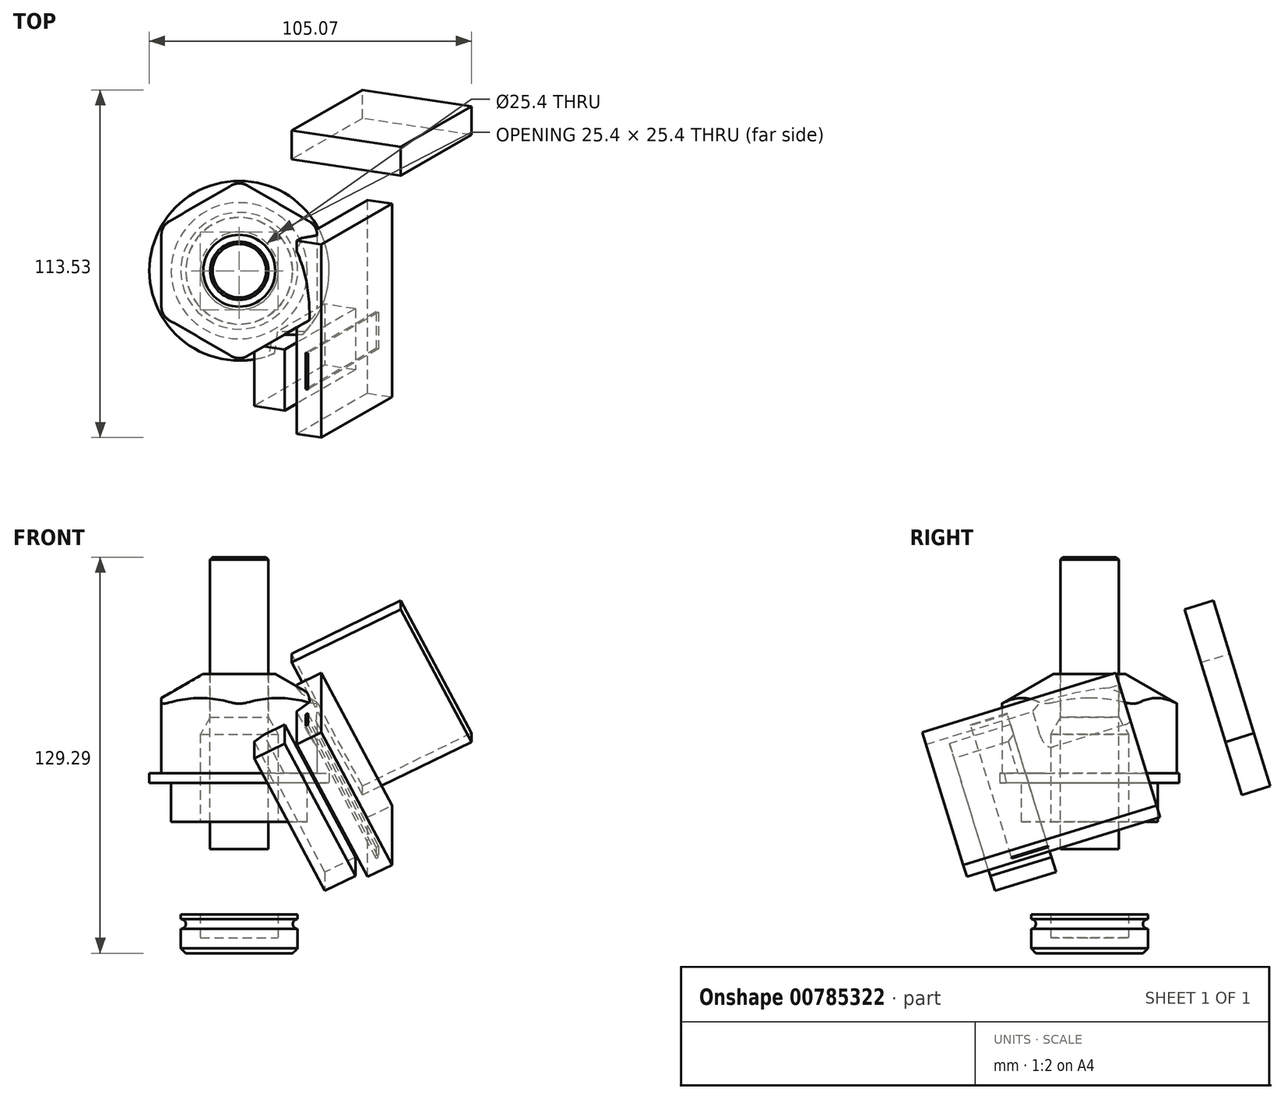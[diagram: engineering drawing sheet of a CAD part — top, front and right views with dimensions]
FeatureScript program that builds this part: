
annotation { "Feature Type Name" : "Feature", "Feature Type Description" : "" }
export const myFeature = defineFeature(function(context is Context, id is Id, definition is map)
    precondition{}
    {
        {
            var Q0;
            Q0=qCreatedBy(makeId("Top.planeOp"),FACE);
            var sketch = newSketch(context, id + "F0", { "sketchPlane" : qUnion([Q0])});
            skCircle(sketch, "E0", {"center": v(0, 0) * mm, "radius": 29.33 * mm});
            skLineSegment(sketch, "E1", {"start": v(0, 29.33) * mm, "end": v(0, -29.33) * mm, "construction": true});
            skLineSegment(sketch, "E2", {"start": v(-25.4, 14.66) * mm, "end": v(25.4, -14.66) * mm, "construction": true});
            skLineSegment(sketch, "E3", {"start": v(-25.4, -14.66) * mm, "end": v(25.4, 14.66) * mm, "construction": true});
            skLineSegment(sketch, "E4", {"start": v(-25.4, 14.66) * mm, "end": v(0, 29.33) * mm});
            skLineSegment(sketch, "E5", {"start": v(0, 29.33) * mm, "end": v(25.4, 14.66) * mm});
            skLineSegment(sketch, "E6", {"start": v(25.4, 14.66) * mm, "end": v(25.4, -14.66) * mm});
            skLineSegment(sketch, "E7", {"start": v(25.4, -14.66) * mm, "end": v(0, -29.33) * mm});
            skLineSegment(sketch, "E8", {"start": v(0, -29.33) * mm, "end": v(-25.4, -14.66) * mm});
            skLineSegment(sketch, "E9", {"start": v(-25.4, -14.66) * mm, "end": v(-25.4, 14.66) * mm});
            skCircle(sketch, "E10", {"center": v(0, 0) * mm, "radius": 7.94 * mm});
            skSolve(sketch);
        }
        {
            var Q0;
            Q0=makeQuery(id+"F0.imprint","IMPRINT",FACE,{"disambiguationData":[TD([[makeQuery(id+"F0.imprint","IMPRINT",EDGE,{"derivedFrom":sQuery(id+"F0.wireOp",EDGE,"E10")}),1.0]])]});
            var Q1;
            Q1=makeQuery(id+"F0.imprint","IMPRINT",FACE,{"disambiguationData":[TD([[makeQuery(id+"F0.imprint","IMPRINT",EDGE,{"derivedFrom":sQuery(id+"F0.wireOp",EDGE,"E4")}),-1.0]])]});
            extrude(context, id + "F1", {"entities" : qUnion([Q0, Q1]), "depth" : 35.56 * mm});
        }
        {
            var Q0;
            {var subQ0=sQuery(id+"F0.wireOp",EDGE,"E8");Q0=makeQuery(id+"F0.imprint","IMPRINT",FACE,{"disambiguationData":[TD([[makeQuery(id+"F0.imprint","IMPRINT",EDGE,{"derivedFrom":subQ0}),1.0]])]});}
            var Q1;
            {var subQ0=sQuery(id+"F0.wireOp",EDGE,"E7");Q1=makeQuery(id+"F0.imprint","IMPRINT",FACE,{"disambiguationData":[TD([[makeQuery(id+"F0.imprint","IMPRINT",EDGE,{"derivedFrom":subQ0}),1.0]])]});}
            var Q2;
            {var subQ0=sQuery(id+"F0.wireOp",EDGE,"E6");Q2=makeQuery(id+"F0.imprint","IMPRINT",FACE,{"disambiguationData":[TD([[makeQuery(id+"F0.imprint","IMPRINT",EDGE,{"derivedFrom":subQ0}),1.0]])]});}
            var Q3;
            Q3=makeQuery(id+"F0.imprint","IMPRINT",FACE,{"disambiguationData":[TD([[makeQuery(id+"F0.imprint","IMPRINT",EDGE,{"derivedFrom":sQuery(id+"F0.wireOp",EDGE,"E4")}),-1.0]])]});
            var Q4;
            {var subQ0=sQuery(id+"F0.wireOp",EDGE,"E5");Q4=makeQuery(id+"F0.imprint","IMPRINT",FACE,{"disambiguationData":[TD([[makeQuery(id+"F0.imprint","IMPRINT",EDGE,{"derivedFrom":subQ0}),1.0]])]});}
            var Q5;
            {var subQ0=sQuery(id+"F0.wireOp",EDGE,"E4");Q5=makeQuery(id+"F0.imprint","IMPRINT",FACE,{"disambiguationData":[TD([[makeQuery(id+"F0.imprint","IMPRINT",EDGE,{"derivedFrom":subQ0}),1.0]])]});}
            var Q6;
            {var subQ0=sQuery(id+"F0.wireOp",EDGE,"E9");Q6=makeQuery(id+"F0.imprint","IMPRINT",FACE,{"disambiguationData":[TD([[makeQuery(id+"F0.imprint","IMPRINT",EDGE,{"derivedFrom":subQ0}),1.0]])]});}
            extrude(context, id + "F2", {"entities" : qUnion([Q0, Q1, Q2, Q3, Q4, Q5, Q6]), "operationType" : NewBodyOperationType.ADD, "depth" : 3.17 * mm});
        }
        {
            var Q0;
            Q0=makeQuery(id+"F1.opExtrude","SWEPT_EDGE",EDGE,{"disambiguationData":[OSD([sQuery(id+"F0.wireOp",EDGE,"E0"),sQuery(id+"F0.wireOp",EDGE,"E7"),sQuery(id+"F0.wireOp",EDGE,"E8")])]});
            var Q1;
            Q1=makeQuery(id+"F1.opExtrude","SWEPT_EDGE",EDGE,{"disambiguationData":[OSD([sQuery(id+"F0.wireOp",EDGE,"E0"),sQuery(id+"F0.wireOp",EDGE,"E6"),sQuery(id+"F0.wireOp",EDGE,"E7")])]});
            var Q2;
            Q2=makeQuery(id+"F1.opExtrude","SWEPT_EDGE",EDGE,{"disambiguationData":[OSD([sQuery(id+"F0.wireOp",EDGE,"E0"),sQuery(id+"F0.wireOp",EDGE,"E5"),sQuery(id+"F0.wireOp",EDGE,"E6")])]});
            var Q3;
            Q3=makeQuery(id+"F1.opExtrude","SWEPT_EDGE",EDGE,{"disambiguationData":[OSD([sQuery(id+"F0.wireOp",EDGE,"E0"),sQuery(id+"F0.wireOp",EDGE,"E4"),sQuery(id+"F0.wireOp",EDGE,"E5")])]});
            var Q4;
            Q4=makeQuery(id+"F1.opExtrude","SWEPT_EDGE",EDGE,{"disambiguationData":[OSD([sQuery(id+"F0.wireOp",EDGE,"E0"),sQuery(id+"F0.wireOp",EDGE,"E4"),sQuery(id+"F0.wireOp",EDGE,"E9")])]});
            var Q5;
            Q5=makeQuery(id+"F1.opExtrude","SWEPT_EDGE",EDGE,{"disambiguationData":[OSD([sQuery(id+"F0.wireOp",EDGE,"E0"),sQuery(id+"F0.wireOp",EDGE,"E8"),sQuery(id+"F0.wireOp",EDGE,"E9")])]});
            fillet(context, id + "F3", {"entities" : qUnion([Q0, Q1, Q2, Q3, Q4, Q5]), "radius" : 5.08 * mm, "tangentPropagation" : true, "allowEdgeOverflow" : false});
        }
        {
            var Q0;
            Q0=qCreatedBy(makeId("Right.planeOp"),FACE);
            var sketch = newSketch(context, id + "F4", { "sketchPlane" : qUnion([Q0])});
            skLineSegment(sketch, "E11", {"start": v(0, 52) * mm, "end": v(0, 0) * mm, "construction": true});
            skLineSegment(sketch, "E12", {"start": v(11.73, 35.56) * mm, "end": v(35.4, 21.9) * mm});
            skLineSegment(sketch, "E13", {"start": v(35.4, 21.9) * mm, "end": v(35.4, 35.56) * mm});
            skLineSegment(sketch, "E14", {"start": v(35.4, 35.56) * mm, "end": v(11.73, 35.56) * mm});
            skLineSegment(sketch, "E15.0", {"start": v(11.73, 35.56) * mm, "end": v(-11.73, 35.56) * mm});
            skLineSegment(sketch, "E16.bottom", {"start": v(0, 0) * mm, "end": v(22.23, 0) * mm});
            skLineSegment(sketch, "E16.top", {"start": v(0, -12.7) * mm, "end": v(22.23, -12.7) * mm});
            skLineSegment(sketch, "E16.left", {"start": v(0, 0) * mm, "end": v(0, -12.7) * mm});
            skLineSegment(sketch, "E16.right", {"start": v(22.23, 0) * mm, "end": v(22.23, -12.7) * mm});
            skLineSegment(sketch, "E17.bottom", {"start": v(0, -12.7) * mm, "end": v(19.05, -12.7) * mm});
            skLineSegment(sketch, "E17.top", {"start": v(0, -27.69) * mm, "end": v(19.05, -27.69) * mm});
            skLineSegment(sketch, "E17.left", {"start": v(0, -12.7) * mm, "end": v(0, -27.69) * mm});
            skLineSegment(sketch, "E17.right", {"start": v(19.05, -12.7) * mm, "end": v(19.05, -27.69) * mm});
            skLineSegment(sketch, "E18.bottom", {"start": v(17.78, -27.69) * mm, "end": v(0, -27.69) * mm});
            skLineSegment(sketch, "E18.top", {"start": v(17.78, -42.93) * mm, "end": v(0, -42.93) * mm});
            skLineSegment(sketch, "E18.left", {"start": v(17.78, -27.69) * mm, "end": v(17.78, -42.93) * mm});
            skLineSegment(sketch, "E18.right", {"start": v(0, -27.69) * mm, "end": v(0, -42.93) * mm});
            skLineSegment(sketch, "E19.bottom", {"start": v(0, -42.93) * mm, "end": v(19.05, -42.93) * mm});
            skLineSegment(sketch, "E19.top", {"start": v(0, -55.63) * mm, "end": v(19.05, -55.63) * mm});
            skLineSegment(sketch, "E19.left", {"start": v(0, -42.93) * mm, "end": v(0, -55.63) * mm});
            skLineSegment(sketch, "E19.right", {"start": v(19.05, -42.93) * mm, "end": v(19.05, -55.63) * mm});
            skCircle(sketch, "E20", {"center": v(19.05, -24.51) * mm, "radius": 1.59 * mm});
            skCircle(sketch, "E21", {"center": v(19.05, -46.1) * mm, "radius": 1.59 * mm});
            skCircle(sketch, "E22", {"center": v(0, -17.46) * mm, "radius": 3.18 * mm});
            skCircle(sketch, "E23", {"center": v(0, -35.3) * mm, "radius": 3.18 * mm});
            skSolve(sketch);
        }
        {
            var Q0;
            Q0=makeQuery(id+"F4.imprint","IMPRINT",FACE,{"disambiguationData":[TD([[makeQuery(id+"F4.imprint","IMPRINT",EDGE,{"derivedFrom":sQuery(id+"F4.wireOp",EDGE,"E12")}),1.0]])]});
            var Q1;
            Q1=sQuery(id+"F4.wireOp",EDGE,"E11");
            revolve(context, id + "F5", {"operationType" : NewBodyOperationType.REMOVE, "entities" : qUnion([Q0]), "axis" : qUnion([Q1]), "revolveType" : RevolveType.FULL, "oppositeDirection" : true});
        }
        {
            var Q0;
            {var subQ7=sQuery(id+"F4.wireOp",EDGE,"E18.bottom");Q0=makeQuery(id+"F4.imprint","IMPRINT",FACE,{"disambiguationData":[TD([[makeQuery(id+"F4.imprint","IMPRINT",EDGE,{"derivedFrom":subQ7}),1.0]])]});}
            var Q1;
            {var subQ10=sQuery(id+"F4.wireOp",EDGE,"E17.bottom");Q1=makeQuery(id+"F4.imprint","IMPRINT",FACE,{"disambiguationData":[TD([[makeQuery(id+"F4.imprint","IMPRINT",EDGE,{"derivedFrom":subQ10}),-1.0]])]});}
            var Q2;
            Q2=makeQuery(id+"F4.imprint","IMPRINT",FACE,{"disambiguationData":[TD([[makeQuery(id+"F4.imprint","IMPRINT",EDGE,{"derivedFrom":sQuery(id+"F4.wireOp",EDGE,"E16.bottom")}),-1.0]])]});
            var Q3;
            {var subQ4=sQuery(id+"F4.wireOp",EDGE,"E19.top");Q3=makeQuery(id+"F4.imprint","IMPRINT",FACE,{"disambiguationData":[TD([[makeQuery(id+"F4.imprint","IMPRINT",EDGE,{"derivedFrom":subQ4}),1.0]])]});}
            var Q4;
            Q4=sQuery(id+"F4.wireOp",EDGE,"E11");
            revolve(context, id + "F6", {"operationType" : NewBodyOperationType.ADD, "entities" : qUnion([Q0, Q1, Q2, Q3]), "axis" : qUnion([Q4]), "revolveType" : RevolveType.FULL});
        }
        {
            var Q0;
            Q0=makeQuery(id+"F6.opRevolve","SWEPT_EDGE",EDGE,{"disambiguationData":[OSD([sQuery(id+"F4.wireOp",EDGE,"E19.top"),sQuery(id+"F4.wireOp",EDGE,"E19.right")])]});
            chamfer(context, id + "F7", {"entities" : qUnion([Q0]), "width" : 1.59 * mm, "tangentPropagation" : true});
        }
        {
            var Q0;
            {var subQ0=sQuery(id+"F4.wireOp",EDGE,"E16.right");var subQ1=sQuery(id+"F4.wireOp",EDGE,"E20");var subQ3=makeQuery(id+"F4.imprint","INTERSECT",VERTEX,{"disambiguationData":[OD(0.0)],"derivedFrom":[subQ0,subQ1]});Q0=makeQuery(id+"F4.imprint","IMPRINT",FACE,{"disambiguationData":[TD([[makeQuery(id+"F4.imprint","SKETCH_ENTITY",EDGE,{"disambiguationData":[TD([[subQ3,-1.0]])],"sketchEntityId":"E16.right"}),1.0]])]});}
            var Q1;
            {var subQ0=sQuery(id+"F4.wireOp",EDGE,"E20");var subQ1=sQuery(id+"F4.wireOp",EDGE,"E17.right");var subQ3=makeQuery(id+"F4.imprint","INTERSECT",VERTEX,{"disambiguationData":[OD(0.0)],"derivedFrom":[subQ1,subQ0]});Q1=makeQuery(id+"F4.imprint","IMPRINT",FACE,{"disambiguationData":[TD([[makeQuery(id+"F4.imprint","IMPRINT",EDGE,{"disambiguationData":[TD([[subQ3,-1.0]])],"derivedFrom":subQ1}),-1.0]])]});}
            var Q2;
            {var subQ0=sQuery(id+"F4.wireOp",EDGE,"E20");var subQ1=sQuery(id+"F4.wireOp",EDGE,"E17.right");var subQ3=makeQuery(id+"F4.imprint","INTERSECT",VERTEX,{"disambiguationData":[OD(0.0)],"derivedFrom":[subQ1,subQ0]});Q2=makeQuery(id+"F4.imprint","IMPRINT",FACE,{"disambiguationData":[TD([[makeQuery(id+"F4.imprint","IMPRINT",EDGE,{"disambiguationData":[TD([[subQ3,-1.0]])],"derivedFrom":subQ1}),1.0]])]});}
            var Q3;
            Q3=sQuery(id+"F4.wireOp",EDGE,"E11");
            revolve(context, id + "F8", {"entities" : qUnion([Q0, Q1, Q2]), "axis" : qUnion([Q3]), "revolveType" : RevolveType.FULL});
        }
        {
            var Q0;
            {var subQ0=sQuery(id+"F4.wireOp",EDGE,"E22");var subQ1=sQuery(id+"F4.wireOp",EDGE,"E17.left");var subQ3=makeQuery(id+"F4.imprint","INTERSECT",VERTEX,{"disambiguationData":[OD(0.0)],"derivedFrom":[subQ1,subQ0]});Q0=makeQuery(id+"F4.imprint","IMPRINT",FACE,{"disambiguationData":[TD([[makeQuery(id+"F4.imprint","IMPRINT",EDGE,{"disambiguationData":[TD([[subQ3,-1.0]])],"derivedFrom":subQ1}),-1.0]])]});}
            var Q1;
            {var subQ0=sQuery(id+"F4.wireOp",EDGE,"E22");var subQ1=sQuery(id+"F4.wireOp",EDGE,"E17.left");var subQ3=makeQuery(id+"F4.imprint","INTERSECT",VERTEX,{"disambiguationData":[OD(0.0)],"derivedFrom":[subQ1,subQ0]});Q1=makeQuery(id+"F4.imprint","IMPRINT",FACE,{"disambiguationData":[TD([[makeQuery(id+"F4.imprint","IMPRINT",EDGE,{"disambiguationData":[TD([[subQ3,-1.0]])],"derivedFrom":subQ1}),1.0]])]});}
            var Q2;
            {var subQ0=sQuery(id+"F4.wireOp",EDGE,"E23");var subQ1=sQuery(id+"F4.wireOp",EDGE,"E18.right");var subQ3=makeQuery(id+"F4.imprint","INTERSECT",VERTEX,{"disambiguationData":[OD(0.0)],"derivedFrom":[subQ1,subQ0]});Q2=makeQuery(id+"F4.imprint","IMPRINT",FACE,{"disambiguationData":[TD([[makeQuery(id+"F4.imprint","IMPRINT",EDGE,{"disambiguationData":[TD([[subQ3,-1.0]])],"derivedFrom":subQ1}),-1.0]])]});}
            var Q3;
            {var subQ0=sQuery(id+"F4.wireOp",EDGE,"E23");var subQ1=sQuery(id+"F4.wireOp",EDGE,"E18.right");var subQ3=makeQuery(id+"F4.imprint","INTERSECT",VERTEX,{"disambiguationData":[OD(0.0)],"derivedFrom":[subQ1,subQ0]});Q3=makeQuery(id+"F4.imprint","IMPRINT",FACE,{"disambiguationData":[TD([[makeQuery(id+"F4.imprint","IMPRINT",EDGE,{"disambiguationData":[TD([[subQ3,-1.0]])],"derivedFrom":subQ1}),1.0]])]});}
            extrude(context, id + "F9", {"entities" : qUnion([Q0, Q1, Q2, Q3]), "operationType" : NewBodyOperationType.REMOVE, "endBound" : BoundingType.THROUGH_ALL, "depth" : 25.4 * mm});
        }
        {
            var Q0;
            Q0=qCreatedBy(makeId("Right.planeOp"),FACE);
            var sketch = newSketch(context, id + "F10", { "sketchPlane" : qUnion([Q0])});
            skLineSegment(sketch, "E24", {"start": v(0, 73.66) * mm, "end": v(0, -50.55) * mm});
            skLineSegment(sketch, "E25", {"start": v(0, -50.55) * mm, "end": v(12.7, -50.55) * mm});
            skLineSegment(sketch, "E26", {"start": v(12.7, -50.55) * mm, "end": v(12.7, 15.88) * mm});
            skLineSegment(sketch, "E27", {"start": v(12.7, 15.88) * mm, "end": v(0, 15.88) * mm});
            skLineSegment(sketch, "E28", {"start": v(9.53, -21.6) * mm, "end": v(9.53, 73.66) * mm});
            skLineSegment(sketch, "E29", {"start": v(9.52, 73.66) * mm, "end": v(0, 73.66) * mm});
            skLineSegment(sketch, "E30", {"start": v(9.53, 21.37) * mm, "end": v(12.7, 15.88) * mm});
            skLineSegment(sketch, "E31.rect.bottom", {"start": v(12.7, -27.94) * mm, "end": v(-12.7, -27.94) * mm});
            skLineSegment(sketch, "E31.rect.top", {"start": v(12.7, -21.59) * mm, "end": v(-12.7, -21.59) * mm});
            skLineSegment(sketch, "E31.rect.left", {"start": v(12.7, -27.94) * mm, "end": v(12.7, -21.59) * mm});
            skLineSegment(sketch, "E31.rect.right", {"start": v(-12.7, -27.94) * mm, "end": v(-12.7, -21.59) * mm});
            skPoint(sketch, "E31.rect.middle", {"position": v(0, -24.77) * mm});
            skSolve(sketch);
        }
        {
            var Q0;
            {var subQ0=sQuery(id+"F10.wireOp",EDGE,"E29");Q0=makeQuery(id+"F10.imprint","IMPRINT",FACE,{"disambiguationData":[TD([[makeQuery(id+"F10.imprint","IMPRINT",EDGE,{"derivedFrom":subQ0}),1.0]])]});}
            var Q1;
            {var subQ0=sQuery(id+"F10.wireOp",EDGE,"E30");Q1=makeQuery(id+"F10.imprint","IMPRINT",FACE,{"disambiguationData":[TD([[makeQuery(id+"F10.imprint","IMPRINT",EDGE,{"derivedFrom":subQ0}),-1.0]])]});}
            var Q2;
            {var subQ1=sQuery(id+"F10.wireOp",EDGE,"E24");var subQ5=sQuery(id+"F10.wireOp",EDGE,"E27");var subQ7=makeQuery(id+"F10.imprint","INTERSECT",VERTEX,{"derivedFrom":[subQ1,subQ5]});Q2=makeQuery(id+"F10.imprint","IMPRINT",FACE,{"disambiguationData":[TD([[makeQuery(id+"F10.imprint","IMPRINT",EDGE,{"disambiguationData":[TD([[subQ7,-1.0]])],"derivedFrom":subQ1}),1.0]])]});}
            var Q3;
            {var subQ0=sQuery(id+"F10.wireOp",EDGE,"E31.rect.top");var subQ3=sQuery(id+"F10.wireOp",EDGE,"E28");var subQ4=makeQuery(id+"F10.imprint","INTERSECT",VERTEX,{"derivedFrom":[subQ3,subQ0]});Q3=makeQuery(id+"F10.imprint","IMPRINT",FACE,{"disambiguationData":[TD([[makeQuery(id+"F10.imprint","IMPRINT",EDGE,{"disambiguationData":[TD([[subQ4,-1.0]])],"derivedFrom":subQ3}),-1.0]])]});}
            var Q4;
            {var subQ5=sQuery(id+"F10.wireOp",EDGE,"E25");Q4=makeQuery(id+"F10.imprint","IMPRINT",FACE,{"disambiguationData":[TD([[makeQuery(id+"F10.imprint","IMPRINT",EDGE,{"derivedFrom":subQ5}),1.0]])]});}
            var Q5;
            {var subQ0=sQuery(id+"F10.wireOp",EDGE,"E31.rect.left");Q5=makeQuery(id+"F10.imprint","IMPRINT",FACE,{"disambiguationData":[TD([[makeQuery(id+"F10.imprint","IMPRINT",EDGE,{"derivedFrom":subQ0}),1.0]])]});}
            var Q6;
            Q6=sQuery(id+"F10.wireOp",EDGE,"E24");
            revolve(context, id + "F11", {"operationType" : NewBodyOperationType.REMOVE, "entities" : qUnion([Q0, Q1, Q2, Q3, Q4, Q5]), "axis" : qUnion([Q6]), "revolveType" : RevolveType.FULL, "oppositeDirection" : true});
        }
        {
            var Q0;
            {var subQ0=sQuery(id+"F10.wireOp",EDGE,"E29");Q0=makeQuery(id+"F10.imprint","IMPRINT",FACE,{"disambiguationData":[TD([[makeQuery(id+"F10.imprint","IMPRINT",EDGE,{"derivedFrom":subQ0}),1.0]])]});}
            var Q1;
            {var subQ1=sQuery(id+"F10.wireOp",EDGE,"E24");var subQ5=sQuery(id+"F10.wireOp",EDGE,"E27");var subQ7=makeQuery(id+"F10.imprint","INTERSECT",VERTEX,{"derivedFrom":[subQ1,subQ5]});Q1=makeQuery(id+"F10.imprint","IMPRINT",FACE,{"disambiguationData":[TD([[makeQuery(id+"F10.imprint","IMPRINT",EDGE,{"disambiguationData":[TD([[subQ7,-1.0]])],"derivedFrom":subQ1}),1.0]])]});}
            var Q2;
            {var subQ0=sQuery(id+"F10.wireOp",EDGE,"E31.rect.left");Q2=makeQuery(id+"F10.imprint","IMPRINT",FACE,{"disambiguationData":[TD([[makeQuery(id+"F10.imprint","IMPRINT",EDGE,{"derivedFrom":subQ0}),1.0]])]});}
            var Q3;
            Q3=sQuery(id+"F10.wireOp",EDGE,"E24");
            revolve(context, id + "F12", {"entities" : qUnion([Q0, Q1, Q2]), "axis" : qUnion([Q3]), "revolveType" : RevolveType.FULL});
        }
        {
            var Q0;
            Q0=makeQuery(id+"F12.opRevolve","SWEPT_EDGE",EDGE,{"disambiguationData":[OSD([sQuery(id+"F10.wireOp",EDGE,"E28"),sQuery(id+"F10.wireOp",EDGE,"E29")])]});
            chamfer(context, id + "F13", {"entities" : qUnion([Q0]), "width" : 0.8 * mm, "tangentPropagation" : true});
        }
        {
            var Q0;
            Q0=makeQuery(id+"F1.opExtrude","SWEPT_FACE",FACE,{"disambiguationData":[OSD([sQuery(id+"F0.wireOp",EDGE,"E7")])]});
            var sketch = newSketch(context, id + "F14", { "sketchPlane" : qUnion([Q0])});
            skLineSegment(sketch, "E32", {"start": v(0, 18.96) * mm, "end": v(11.73, 26.18) * mm});
            skSolve(sketch);
        }
        {
            var Q0;
            Q0=qSketchRegion(id+"F14",true);
            var Q1;
            Q1=sQuery(id+"F14.wireOp",EDGE,"E32");
            extrude(context, id + "F15", {"entities" : qUnion([Q0]), "bodyType" : ToolBodyType.SURFACE, "surfaceEntities" : qUnion([Q1]), "depth" : 25.4 * mm, "offsetDistance" : 25.4 * mm});
        }
        {
            var Q0;
            Q0=makeQuery(id+"F15.opExtrude","SWEPT_FACE",FACE,{"disambiguationData":[OSD([sQuery(id+"F14.wireOp",EDGE,"E32")])]});
            var sketch = newSketch(context, id + "F16", { "sketchPlane" : qUnion([Q0])});
            skLineSegment(sketch, "E33.bottom", {"start": v(32.52, 19) * mm, "end": v(33.33, 19) * mm});
            skLineSegment(sketch, "E33.top", {"start": v(32.52, 31.47) * mm, "end": v(33.33, 31.47) * mm});
            skLineSegment(sketch, "E33.left", {"start": v(32.52, 19) * mm, "end": v(32.52, 31.47) * mm});
            skLineSegment(sketch, "E33.right", {"start": v(33.33, 19) * mm, "end": v(33.33, 31.47) * mm});
            skLineSegment(sketch, "E34.bottom", {"start": v(24.88, 19) * mm, "end": v(13.7, 19) * mm});
            skLineSegment(sketch, "E34.top", {"start": v(24.88, 39.84) * mm, "end": v(13.7, 39.84) * mm});
            skLineSegment(sketch, "E34.left", {"start": v(24.88, 19) * mm, "end": v(24.88, 39.84) * mm});
            skLineSegment(sketch, "E34.right", {"start": v(13.7, 19) * mm, "end": v(13.7, 39.84) * mm});
            skLineSegment(sketch, "E35.bottom", {"start": v(29.3, 47.23) * mm, "end": v(38.25, 47.23) * mm});
            skLineSegment(sketch, "E35.top", {"start": v(29.3, -18.76) * mm, "end": v(38.25, -18.76) * mm});
            skLineSegment(sketch, "E35.left", {"start": v(29.3, 47.23) * mm, "end": v(29.3, -18.76) * mm});
            skLineSegment(sketch, "E35.right", {"start": v(38.25, 47.23) * mm, "end": v(38.25, -18.76) * mm});
            skLineSegment(sketch, "E36.bottom", {"start": v(67.35, -46.34) * mm, "end": v(27.42, -46.34) * mm});
            skLineSegment(sketch, "E36.top", {"start": v(67.35, -56.1) * mm, "end": v(27.42, -56.1) * mm});
            skLineSegment(sketch, "E36.left", {"start": v(67.35, -46.34) * mm, "end": v(67.35, -56.1) * mm});
            skLineSegment(sketch, "E36.right", {"start": v(27.42, -46.34) * mm, "end": v(27.42, -56.1) * mm});
            skSolve(sketch);
        }
        {
            var Q0;
            Q0=qSketchRegion(id+"F16",true);
            extrude(context, id + "F17", {"entities" : qUnion([Q0]), "operationType" : NewBodyOperationType.ADD, "depth" : 50.8 * mm, "offsetDistance" : 25.4 * mm});
        }
    });
